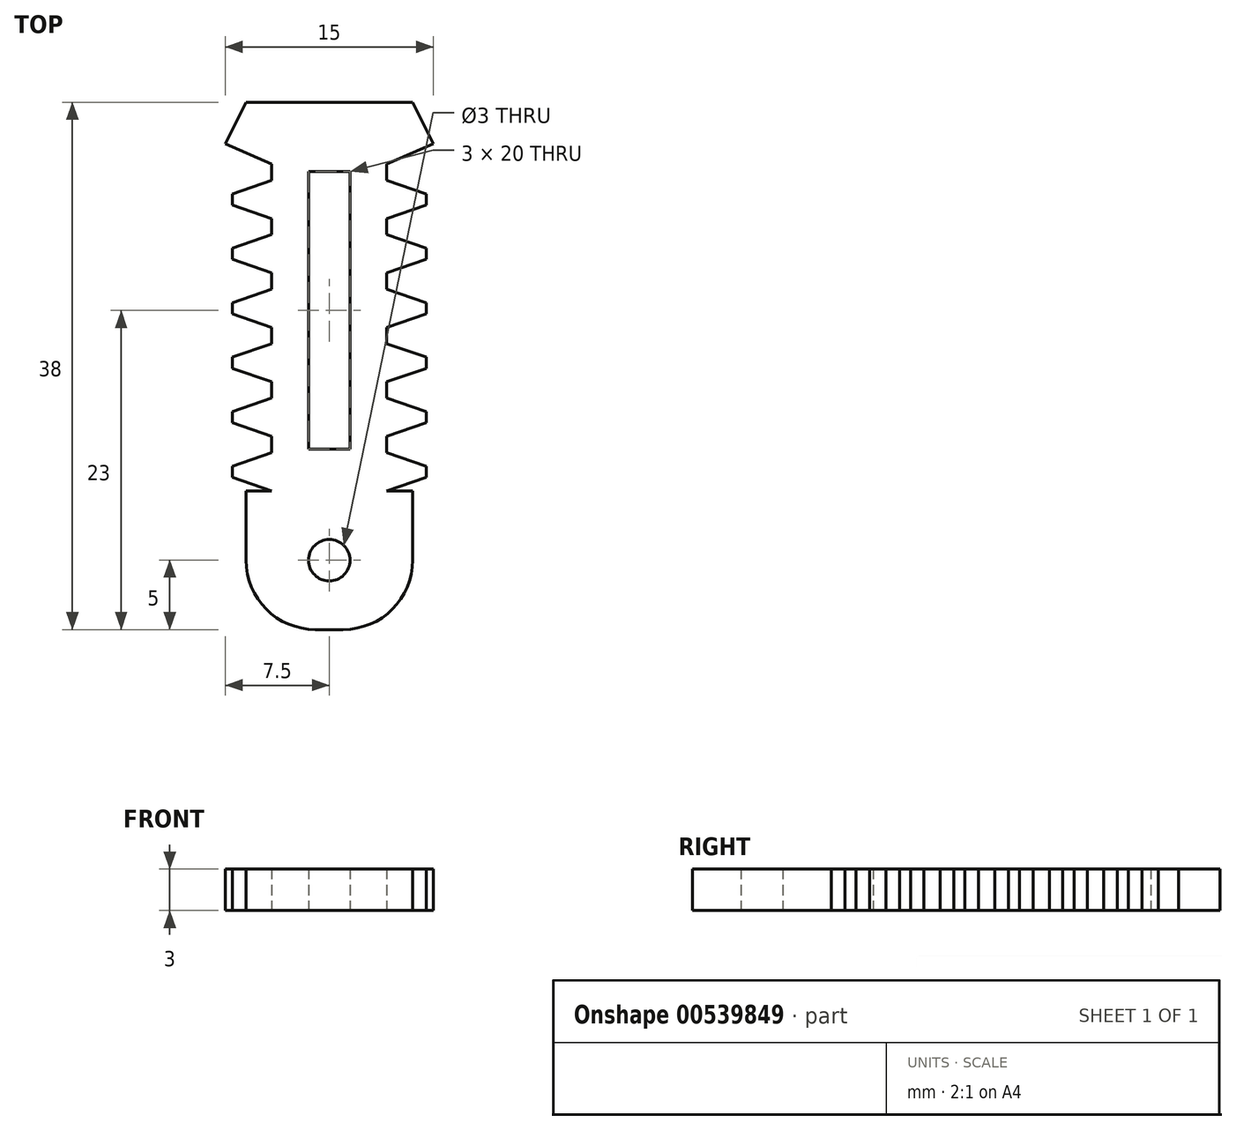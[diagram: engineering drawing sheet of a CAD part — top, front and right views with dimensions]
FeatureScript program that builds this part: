
annotation { "Feature Type Name" : "Feature", "Feature Type Description" : "" }
export const myFeature = defineFeature(function(context is Context, id is Id, definition is map)
    precondition{}
    {
        {
            var Q0;
            Q0=qCreatedBy(makeId("Top.planeOp"),FACE);
            var sketch = newSketch(context, id + "F0", { "sketchPlane" : qUnion([Q0])});
            skLineSegment(sketch, "E0", {"start": v(-7.5, 0) * mm, "end": v(-6, 0) * mm});
            skLineSegment(sketch, "E1", {"start": v(7.5, 0) * mm, "end": v(7.5, 25) * mm});
            skLineSegment(sketch, "E2", {"start": v(7.5, 25) * mm, "end": v(6, 28) * mm});
            skLineSegment(sketch, "E3", {"start": v(6, 28) * mm, "end": v(-6, 28) * mm});
            skLineSegment(sketch, "E4", {"start": v(-6, 28) * mm, "end": v(-7.5, 25) * mm});
            skLineSegment(sketch, "E5", {"start": v(-7.5, 25) * mm, "end": v(-7.5, 0) * mm});
            skLineSegment(sketch, "E6", {"start": v(0, 0) * mm, "end": v(0, 16.17) * mm, "construction": true});
            skLineSegment(sketch, "E7", {"start": v(-6, 36.25) * mm, "end": v(-6, 28) * mm, "construction": true});
            skLineSegment(sketch, "E8", {"start": v(6, 28) * mm, "end": v(6, 25) * mm, "construction": true});
            skLineSegment(sketch, "E9.top", {"start": v(-1, -10) * mm, "end": v(1, -10) * mm});
            skLineSegment(sketch, "E9.left", {"start": v(-6, 0) * mm, "end": v(-6, -5) * mm});
            skLineSegment(sketch, "E9.right", {"start": v(6, 0) * mm, "end": v(6, -5) * mm});
            skLineSegment(sketch, "E10.trimOffspring", {"start": v(6, 0) * mm, "end": v(7.5, 0) * mm});
            skPoint(sketch, "E11.visualSharp", {"position": v(-6, -10) * mm});
            skArc(sketch, "E11.filletArc", {"start": v(-6, -5) * mm, "mid": v(-4.54, -8.54) * mm, "end": v(-1, -10) * mm});
            skPoint(sketch, "E12.visualSharp", {"position": v(6, -10) * mm});
            skArc(sketch, "E12.filletArc", {"start": v(1, -10) * mm, "mid": v(4.54, -8.54) * mm, "end": v(6, -5) * mm});
            skCircle(sketch, "E13", {"center": v(0, -5) * mm, "radius": 1.5 * mm});
            skLineSegment(sketch, "E14.bottom", {"start": v(1.5, 3) * mm, "end": v(-1.5, 3) * mm});
            skLineSegment(sketch, "E14.top", {"start": v(1.5, 23) * mm, "end": v(-1.5, 23) * mm});
            skLineSegment(sketch, "E14.left", {"start": v(1.5, 3) * mm, "end": v(1.5, 23) * mm});
            skLineSegment(sketch, "E14.right", {"start": v(-1.5, 3) * mm, "end": v(-1.5, 23) * mm});
            skSolve(sketch);
        }
        {
            var Q0;
            Q0=makeQuery(id+"F0.imprint","IMPRINT",FACE,{"disambiguationData":[TD([[makeQuery(id+"F0.imprint","IMPRINT",EDGE,{"derivedFrom":sQuery(id+"F0.wireOp",EDGE,"E0")}),1.0]])]});
            extrude(context, id + "F1", {"entities" : qUnion([Q0]), "depth" : 3 * mm, "offsetDistance" : 25 * mm});
        }
        {
            var Q0;
            Q0=makeQuery(id+"F1.opExtrude","CAP_FACE",FACE,{"disambiguationData":[OSD([sQuery(id+"F0.wireOp",EDGE,"E0"),sQuery(id+"F0.wireOp",EDGE,"E1"),sQuery(id+"F0.wireOp",EDGE,"E2"),sQuery(id+"F0.wireOp",EDGE,"E3"),sQuery(id+"F0.wireOp",EDGE,"E4"),sQuery(id+"F0.wireOp",EDGE,"E5")])],"isStart":true});
            var sketch = newSketch(context, id + "F2", { "sketchPlane" : qUnion([Q0])});
            skLineSegment(sketch, "E15", {"start": v(0, 0) * mm, "end": v(0, -19.37) * mm, "construction": true});
            skLineSegment(sketch, "E16", {"start": v(-4.14, 0) * mm, "end": v(-6.98, -0.98) * mm});
            skLineSegment(sketch, "E17", {"start": v(-6.98, -0.98) * mm, "end": v(-6.98, -1.78) * mm});
            skLineSegment(sketch, "E18", {"start": v(-6.98, -1.78) * mm, "end": v(-4.14, -2.75) * mm});
            skLineSegment(sketch, "E19", {"start": v(-4.14, -2.75) * mm, "end": v(-4.14, -3.92) * mm});
            skLineSegment(sketch, "E20.direction1", {"start": v(-6.98, -1.78) * mm, "end": v(-6.98, -5.7) * mm, "construction": true});
            skLineSegment(sketch, "E21.0.1.0", {"start": v(-4.14, -3.92) * mm, "end": v(-6.98, -4.9) * mm});
            skLineSegment(sketch, "E21.3.1.0", {"start": v(-4.14, -6.68) * mm, "end": v(-4.14, -7.85) * mm});
            skLineSegment(sketch, "E21.6.1.0", {"start": v(-6.98, -5.7) * mm, "end": v(-4.14, -6.68) * mm});
            skLineSegment(sketch, "E21.9.1.0", {"start": v(-6.98, -4.9) * mm, "end": v(-6.98, -5.7) * mm});
            skLineSegment(sketch, "E22.0.2.0", {"start": v(-4.14, -7.85) * mm, "end": v(-6.98, -8.83) * mm});
            skLineSegment(sketch, "E22.3.2.0", {"start": v(-4.14, -10.6) * mm, "end": v(-4.14, -11.77) * mm});
            skLineSegment(sketch, "E22.6.2.0", {"start": v(-6.98, -9.63) * mm, "end": v(-4.14, -10.6) * mm});
            skLineSegment(sketch, "E22.9.2.0", {"start": v(-6.98, -8.83) * mm, "end": v(-6.98, -9.63) * mm});
            skLineSegment(sketch, "E23.0.3.0", {"start": v(-4.14, -11.77) * mm, "end": v(-6.98, -12.75) * mm});
            skLineSegment(sketch, "E23.3.3.0", {"start": v(-4.14, -14.53) * mm, "end": v(-4.14, -15.7) * mm});
            skLineSegment(sketch, "E23.6.3.0", {"start": v(-6.98, -13.55) * mm, "end": v(-4.14, -14.53) * mm});
            skLineSegment(sketch, "E23.9.3.0", {"start": v(-6.98, -12.75) * mm, "end": v(-6.98, -13.55) * mm});
            skLineSegment(sketch, "E24.0.4.0", {"start": v(-4.14, -15.7) * mm, "end": v(-6.98, -16.68) * mm});
            skLineSegment(sketch, "E24.3.4.0", {"start": v(-4.14, -18.45) * mm, "end": v(-4.14, -19.62) * mm});
            skLineSegment(sketch, "E24.6.4.0", {"start": v(-6.98, -17.48) * mm, "end": v(-4.14, -18.45) * mm});
            skLineSegment(sketch, "E24.9.4.0", {"start": v(-6.98, -16.68) * mm, "end": v(-6.98, -17.48) * mm});
            skLineSegment(sketch, "E25.0.5.0", {"start": v(-4.14, -19.62) * mm, "end": v(-6.98, -20.6) * mm});
            skLineSegment(sketch, "E25.3.5.0", {"start": v(-4.14, -22.38) * mm, "end": v(-4.14, -23.55) * mm});
            skLineSegment(sketch, "E25.6.5.0", {"start": v(-6.98, -21.4) * mm, "end": v(-4.14, -22.38) * mm});
            skLineSegment(sketch, "E25.9.5.0", {"start": v(-6.98, -20.6) * mm, "end": v(-6.98, -21.4) * mm});
            skLineSegment(sketch, "E26", {"start": v(-4.14, -23.55) * mm, "end": v(-7.5, -25) * mm});
            skLineSegment(sketch, "E27.MirrorCS", {"start": v(6.98, -0.98) * mm, "end": v(6.98, -1.78) * mm});
            skLineSegment(sketch, "E28.MirrorCS", {"start": v(4.14, -18.45) * mm, "end": v(4.14, -19.62) * mm});
            skLineSegment(sketch, "E29.MirrorCS", {"start": v(4.14, -22.38) * mm, "end": v(4.14, -23.55) * mm});
            skLineSegment(sketch, "E30.MirrorCS", {"start": v(6.98, -20.6) * mm, "end": v(6.98, -21.4) * mm});
            skLineSegment(sketch, "E31.MirrorCS", {"start": v(6.98, -4.9) * mm, "end": v(6.98, -5.7) * mm});
            skLineSegment(sketch, "E32.MirrorCS", {"start": v(4.14, -2.75) * mm, "end": v(4.14, -3.93) * mm});
            skLineSegment(sketch, "E33.MirrorCS", {"start": v(6.98, -12.75) * mm, "end": v(6.98, -13.55) * mm});
            skLineSegment(sketch, "E34.MirrorCS", {"start": v(6.98, -16.68) * mm, "end": v(6.98, -17.48) * mm});
            skLineSegment(sketch, "E35.MirrorCS", {"start": v(6.98, -8.83) * mm, "end": v(6.98, -9.63) * mm});
            skLineSegment(sketch, "E36.MirrorCS", {"start": v(4.14, -10.6) * mm, "end": v(4.14, -11.77) * mm});
            skLineSegment(sketch, "E37.MirrorCS", {"start": v(4.14, -6.68) * mm, "end": v(4.14, -7.85) * mm});
            skLineSegment(sketch, "E38.MirrorCS", {"start": v(4.14, -14.53) * mm, "end": v(4.14, -15.7) * mm});
            skLineSegment(sketch, "E39.MirrorCS", {"start": v(6.98, -21.4) * mm, "end": v(4.14, -22.38) * mm});
            skLineSegment(sketch, "E40.MirrorCS", {"start": v(6.98, -9.63) * mm, "end": v(4.14, -10.6) * mm});
            skLineSegment(sketch, "E41.MirrorCS", {"start": v(4.14, -11.77) * mm, "end": v(6.98, -12.75) * mm});
            skLineSegment(sketch, "E42.MirrorCS", {"start": v(4.14, -7.85) * mm, "end": v(6.98, -8.83) * mm});
            skLineSegment(sketch, "E43.MirrorCS", {"start": v(6.98, -5.7) * mm, "end": v(4.14, -6.68) * mm});
            skLineSegment(sketch, "E44.MirrorCS", {"start": v(4.14, 0) * mm, "end": v(6.98, -0.98) * mm});
            skLineSegment(sketch, "E45.MirrorCS", {"start": v(6.98, -1.78) * mm, "end": v(4.14, -2.75) * mm});
            skLineSegment(sketch, "E46.MirrorCS", {"start": v(6.98, -1.78) * mm, "end": v(6.98, -5.7) * mm, "construction": true});
            skLineSegment(sketch, "E47.MirrorCS", {"start": v(4.14, -3.92) * mm, "end": v(6.98, -4.9) * mm});
            skLineSegment(sketch, "E48.MirrorCS", {"start": v(4.14, -15.7) * mm, "end": v(6.98, -16.68) * mm});
            skLineSegment(sketch, "E49.MirrorCS", {"start": v(4.14, -19.62) * mm, "end": v(6.98, -20.6) * mm});
            skLineSegment(sketch, "E50.MirrorCS", {"start": v(4.14, -23.55) * mm, "end": v(7.5, -25) * mm});
            skLineSegment(sketch, "E51.MirrorCS", {"start": v(6.98, -13.55) * mm, "end": v(4.14, -14.53) * mm});
            skLineSegment(sketch, "E52.MirrorCS", {"start": v(6.98, -17.48) * mm, "end": v(4.14, -18.45) * mm});
            skLineSegment(sketch, "E53", {"start": v(-4.14, 0) * mm, "end": v(-6, 0) * mm});
            skLineSegment(sketch, "E54", {"start": v(4.14, 0) * mm, "end": v(6, 0) * mm});
            skSolve(sketch);
        }
        {
            var Q0;
            {var subQ0=sQuery(id+"F2.wireOp",EDGE,"E16");Q0=makeQuery(id+"F2.imprint","IMPRINT",FACE,{"disambiguationData":[TD([[makeQuery(id+"F2.imprint","IMPRINT",EDGE,{"derivedFrom":subQ0}),-1.0]])]});}
            var Q1;
            Q1=makeQuery(id+"F2.imprint","IMPRINT",FACE,{"disambiguationData":[TD([[makeQuery(id+"F2.imprint","IMPRINT",EDGE,{"derivedFrom":sQuery(id+"F2.wireOp",EDGE,"E27.MirrorCS")}),1.0]])]});
            extrude(context, id + "F3", {"entities" : qUnion([Q0, Q1]), "operationType" : NewBodyOperationType.REMOVE, "oppositeDirection" : true, "depth" : 25 * mm, "offsetDistance" : 25 * mm});
        }
    });
